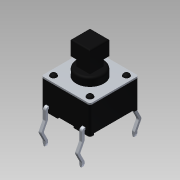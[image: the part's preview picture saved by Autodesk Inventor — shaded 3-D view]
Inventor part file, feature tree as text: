
AUTODESK INVENTOR PART (.ipt)
format: ipt  version: 2015 SP1 (Build 190203100, 203)  size: 372,224 bytes
history: native  units: in
note: dims shown in document units (in); Inventor stores cm internally (conversion verified against a paired STEP export)
features: imported_body x5, chamfer x3, other x2, fillet x1
ambient origin geometry x8: Origin, YZ Plane, XZ Plane, XY Plane, X Axis, Y Axis, Z Axis, Center Point
bodies: Body1 (feature_tree), Body2 (feature_tree), Body3 (feature_tree), Body4 (feature_tree), Body5 (feature_tree)
feature tree (11):
  other  "Cut-Revolve1[2]"
  other  "tactpushbutton1"
  fillet  "Fillet4"  [1 undecoded]
  chamfer  "Chamfer2"  [1 undecoded]
  chamfer  "Chamfer6"  [1 undecoded]
  chamfer  "Chamfer8"  [1 undecoded]
  imported_body  "Base1"
  imported_body  "Base2"
  imported_body  "Base3"
  imported_body  "Base4"
  imported_body  "Base5"
note: 4 required parameter values undecoded (feature->parameter linkage not recoverable at this tier; creation-order binding heuristic only, values carry confidence <= 0.55)
